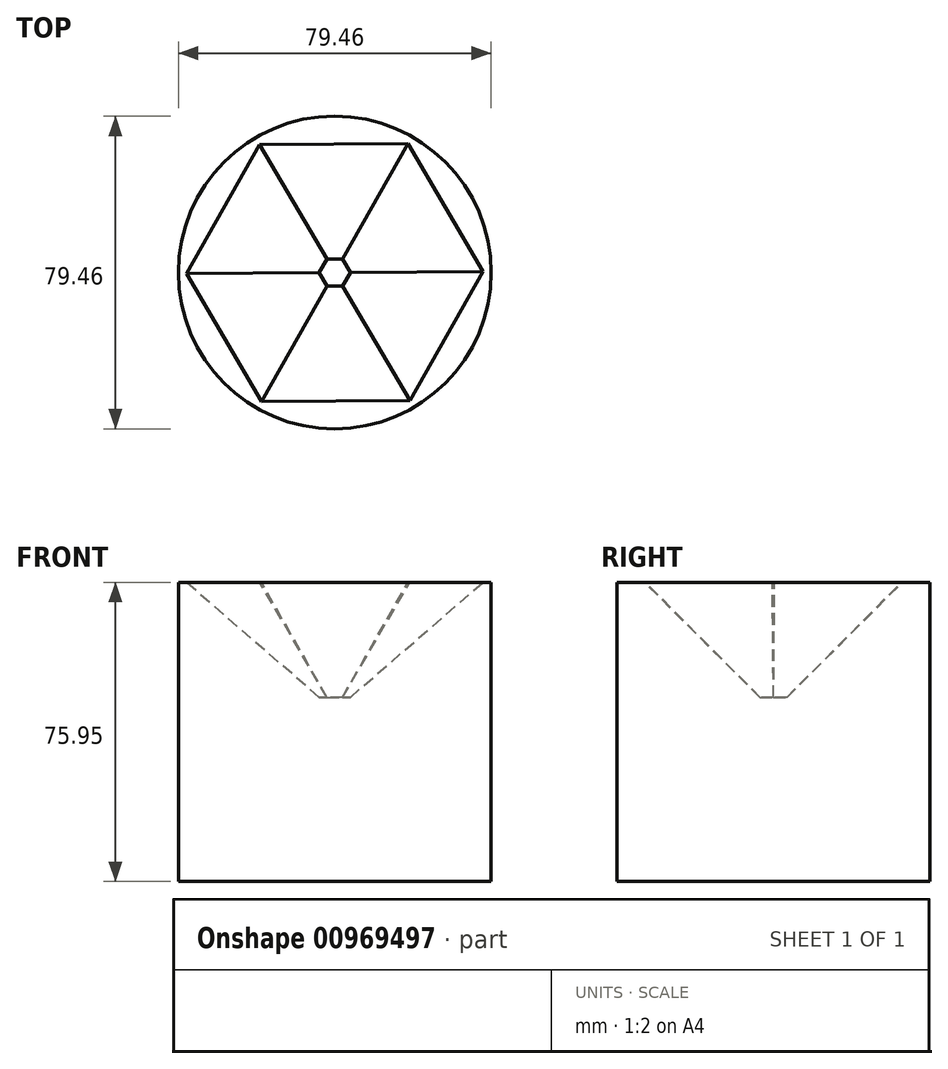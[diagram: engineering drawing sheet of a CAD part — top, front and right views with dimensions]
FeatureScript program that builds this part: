
annotation { "Feature Type Name" : "Feature", "Feature Type Description" : "" }
export const myFeature = defineFeature(function(context is Context, id is Id, definition is map)
    precondition{}
    {
        {
            var Q0;
            Q0=qCreatedBy(makeId("Top.planeOp"),FACE);
            var sketch = newSketch(context, id + "F0", { "sketchPlane" : qUnion([Q0])});
            skCircle(sketch, "E0", {"center": v(0, 0) * mm, "radius": 39.73 * mm});
            skSolve(sketch);
        }
        {
            var Q0;
            Q0=makeQuery(id+"F0.imprint","IMPRINT",FACE,{"disambiguationData":[TD([[makeQuery(id+"F0.imprint","IMPRINT",EDGE,{"derivedFrom":sQuery(id+"F0.wireOp",EDGE,"E0")}),1.0]])]});
            extrude(context, id + "F1", {"entities" : qUnion([Q0]), "depth" : 75.95 * mm, "offsetDistance" : 25.4 * mm});
        }
        {
            var Q0;
            Q0=makeQuery(id+"F1.opExtrude","CAP_FACE",FACE,{"disambiguationData":[OSD([sQuery(id+"F0.wireOp",EDGE,"E0")])],"isStart":false});
            var sketch = newSketch(context, id + "F2", { "sketchPlane" : qUnion([Q0])});
            skCircle(sketch, "E1.cCircle", {"center": v(0, 0) * mm, "radius": 32.63 * mm, "construction": true});
            skLineSegment(sketch, "E1.0", {"start": v(18.6, 32.77) * mm, "end": v(37.67, 0.28) * mm});
            skLineSegment(sketch, "E1.1", {"start": v(37.67, 0.28) * mm, "end": v(19.08, -32.49) * mm});
            skLineSegment(sketch, "E1.2", {"start": v(19.08, -32.49) * mm, "end": v(-18.6, -32.77) * mm});
            skLineSegment(sketch, "E1.3", {"start": v(-18.6, -32.77) * mm, "end": v(-37.67, -0.28) * mm});
            skLineSegment(sketch, "E1.4", {"start": v(-37.67, -0.28) * mm, "end": v(-19.08, 32.49) * mm});
            skLineSegment(sketch, "E1.5", {"start": v(-19.08, 32.49) * mm, "end": v(18.6, 32.77) * mm});
            skPoint(sketch, "E1.0.midPoint", {"position": v(28.13, 16.52) * mm});
            skSolve(sketch);
        }
        {
            var Q0;
            Q0 = qSketchRegion(id + "F2", true);
            extrude(context, id + "F3", {"entities" : qUnion([Q0]), "operationType" : NewBodyOperationType.REMOVE, "oppositeDirection" : true, "depth" : 29.2 * mm, "offsetDistance" : 25.4 * mm, "hasDraft" : true, "draftAngle" : 45 * degree, "draftPullDirection" : true});
        }
    });
